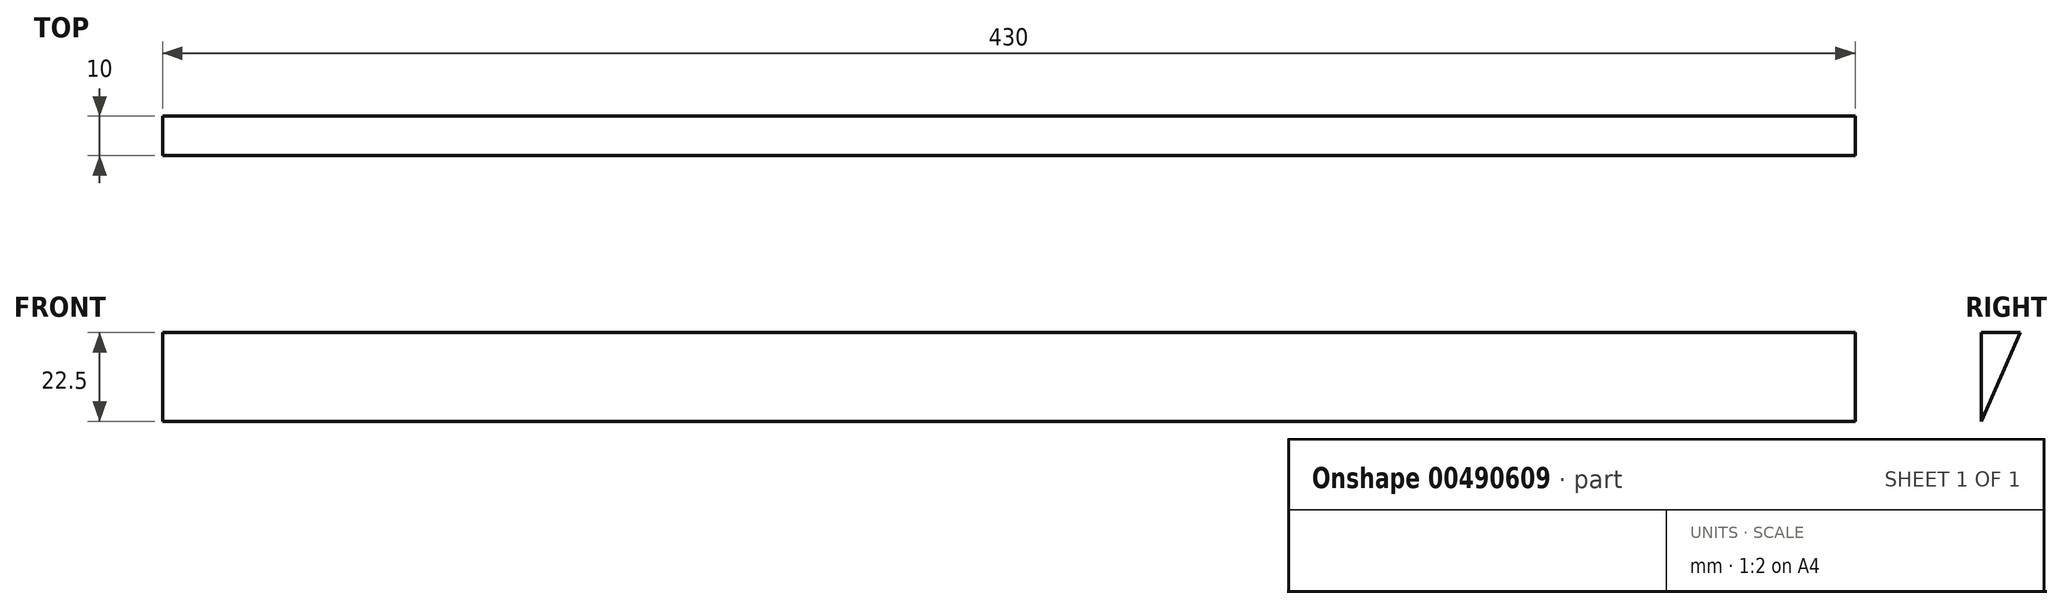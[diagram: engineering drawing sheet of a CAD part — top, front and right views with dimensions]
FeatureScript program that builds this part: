
annotation { "Feature Type Name" : "Feature", "Feature Type Description" : "" }
export const myFeature = defineFeature(function(context is Context, id is Id, definition is map)
    precondition{}
    {
        {
            var Q0;
            Q0=qCreatedBy(makeId("Right.planeOp"),FACE);
            var sketch = newSketch(context, id + "F0", { "sketchPlane" : qUnion([Q0])});
            skLineSegment(sketch, "E0", {"start": v(0, 0) * mm, "end": v(0, 22.5) * mm});
            skLineSegment(sketch, "E1", {"start": v(0, 22.5) * mm, "end": v(10, 22.5) * mm});
            skLineSegment(sketch, "E2", {"start": v(10, 22.5) * mm, "end": v(0, 0) * mm});
            skSolve(sketch);
        }
        {
            var Q0;
            Q0=makeQuery(id+"F0.imprint","IMPRINT",FACE,{"disambiguationData":[TD([[makeQuery(id+"F0.imprint","IMPRINT",EDGE,{"derivedFrom":sQuery(id+"F0.wireOp",EDGE,"E0")}),-1.0]])]});
            extrude(context, id + "F1", {"entities" : qUnion([Q0]), "endBound" : BoundingType.SYMMETRIC, "depth" : 430 * mm});
        }
    });
